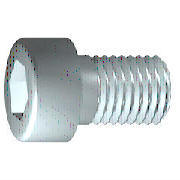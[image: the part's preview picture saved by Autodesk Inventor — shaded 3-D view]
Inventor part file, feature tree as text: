
AUTODESK INVENTOR PART (.ipt)
format: ipt  version: 2016 SP1 (Build 200210100, 210)  size: 182,784 bytes
history: native  units: mm (DEFAULTED — no unit token found)
features: sketch x2, extrude x1, plane x1, fillet x1
ambient origin geometry x7: Origin, YZ Plane, XY Plane, X Axis, Y Axis, Z Axis, Center Point
bodies: Solid1 (feature_tree), Body (feature_tree)
feature tree (5):
  extrude  "Slot"  Depth=1.5876mm
  plane  "Work Plane1"
  fillet  "Fillet2"  Radius=3.175mm
  sketch  "Sketch1"  dims[d1=19.05mm d2=1.5876mm d3=3.175mm]
  sketch  "Sketch2"  dims[d4=1.4478mm d5=60.0deg d6=3.175mm d7=3.175mm d8=2.756963mm d9=5.207mm d10=90.0deg d11=10.0mm d12=0.0mm d13=19.05mm d14=0.0mm d15=0.37846mm d16=0.37846mm d17=0.3048mm d19=0.0mm d26=38.1mm d27=45.0deg d28=0.0mm d29=0.0mm d30=0.127mm]
